# Revit family: Bosch_MechanicalEquipment_GasCondensingBoiler_Condens7000FCascadePair_LowOutput
name_source: partatom
category: Mechanical Equipment
revit_build: Autodesk Revit 2016 (Build: 20151007_0715(x64)
units: mm (PartAtom-declared; Revit-internal decimal feet)

## family parameters
Always vertical = Yes
Cut with Voids When Loaded = No
OmniClass Number = 23.75.00.00
OmniClass Title = Climate Control (HVAC)
Part Type = Normal
Room Calculation Point = No
Round Connector Dimension = Use Diameter
Shared = No
Work Plane-Based = No

## types (1)
- Bosch_MechanicalEquipment_GasCondensingBoiler_Condens7000FCascadePair_LowOutput
    150kW = No
    200-300kW = Yes
    6Monthly = No
    75-100kW = No
    AccessClearanceBottom = 0 mm  [stored 0 ft]
    AccessClearanceTop = 0 mm  [stored 0 ft]
    AirInletConnectionSize = 160
    AirInletHeight = 163 mm  [stored 0.534777 ft]
    AirInletOffset = 195 mm  [stored 0.639764 ft]
    Annually = Annual Service
    Assembly Code = D3020100
    AssetType = Fixed
    BIMObjectName = Bosch_MechanicalEquipment_GasCondensingBoilerCascadePair_Condens7000F_600kW
    BMSLinks = Yes
    BespokeTimeframe = No
    BoilerType1 = Bosch_MechanicalEquipment_GasCondensingBoiler_Condens7000FSingle_LowOutput : 300kW (LH)
    BoilerType2 = Bosch_MechanicalEquipment_GasCondensingBoiler_Condens7000FSingle_LowOutput : 300kW (RH)
    BuildingRegulationsSeasonalEfficiency = 96.8
    BurnerConfiguration = Integral
    CEApproval = CE-0085CS0098
    ClassificationName = Uniclass2015
    ClassificationValue = Pr_60_60_08_34
    CodePerformance = EU Regulations 811/2013, 812/2013, 813/2013 and 814/2013 of Directive 2010/30/EU
    Color = Grey
    CondensateDia = 20 mm  [stored 0.0656168 ft]
    CondensateDrainSize = DN20
    CondensateDrainType = Pipe
    CondensateHeight = 177 mm  [stored 0.580709 ft]
    CondensateOffset = 209 mm  [stored 0.685696 ft]
    Configuration = Cascade Pair Boiler
    Constituents = Aluminium, steel, polymers
    ControlOptions = MX25 or CC 8313
    ControlType = EMS, Volt free, 0-10VDC
    Daily = No
    Description = Higher fuel efficiency, lower environmental impact and exemplary economy - the condensing boiler Condens 7000 F offers you a new level of efficiency in condensing technology. Suitable for multi-family homes and commercial properties, they are the ideal solution for large projects from 75 to 600 kW.
    DocumentationLiterature = https://www.bosch-thermotechnology.com
    DrainCockDia = 15 mm  [stored 0.0492126 ft]
    DrainCockHeight = 498 mm
    DrainConnectionSize = 1/2"
    DrainConnectionType = Threaded
    DurationUnit = Years
    ExpectedLife = 20
    ExternalMaterial = Steel
    Features = Optional retrofittable internet interface and the mobile control of Bosch EasyRemote or HomeCom (Pro).
    Finish = Paint
    FlowAndReturnConnectionSize = DN65
    FlowAndReturnConnectionType = Flange
    FlowOutDepth = 49 mm  [stored 0.160761 ft]
    FlowOutDia = 65 mm  [stored 0.213255 ft]
    FlueOrAirIntakeClassification = OF or RS
    FlueRearDepth = 63 mm
    FlueRearHeight = 765 mm  [stored 2.50984 ft]
    Frequency = 50Hz
    FuelConnectionSize = 1 1/4"
    FuelConnectionType = Threaded
    FullLoadCurrent = 1.46
    FuseRating = 6.3/10
    GasConsumptionRate = 60.4m3/h
    GasHeightOffset = 139 mm  [stored 0.456037 ft]
    GasInDia = 32 mm  [stored 0.104987 ft]
    GasOffset = 478 mm  [stored 1.56824 ft]
    GrossWeight = 544.00 kg
    HasMaintenanceLane = No
    HeatExchangerMaterial = Aluminium
    HeaterOperation = Sealed System
    Height = 1470 mm  [stored 4.82283 ft]
    IPRating = IPX0D
    IfcExportAs = IfcBoiler
    IfcExportType = IfcBoilerTypeEnum.GAS
    Interlocks = Yes
    Keynote = T20/320
    LH = Yes
    LHDrainCockOffset = 495 mm  [stored 1.62402 ft]
    LHFlowOffset = 485 mm  [stored 1.59121 ft]
    LHVSLOffset = 495 mm  [stored 1.62402 ft]
    Length = 1250 mm  [stored 4.10105 ft]
    LocationOfManufacturer = Germany
    MaintenanceRequired0-300Hrs = No
    MaintenanceRequired1001-2000Hrs = No
    MaintenanceRequired2001-4000Hrs = No
    MaintenanceRequired301-600Hrs = No
    MaintenanceRequired4001-8000Hrs = No
    MaintenanceRequired601-1000Hrs = No
    MaintenanceRequired8001-12000Hrs = No
    Manufacturer = Bosch Thermotechnology
    ManufacturerName = Bosch Thermotechnology
    Material = Aluminium, steel, stainless steel,  polymers
    MaximumGasInletPressure = 25mbar
    MaximumOperatingPressure = 6bar
    MaximumPowerConsumption = 672Watts
    MinimumGasInletPressure = 17mbar
    MinimumOperatingPressure = 0.8bar
    MinimumPowerConsumption = 48Watts
    Model = Condens 7000F Gas Condensing Boiler (Cascade Pair)
    ModelNumber = 600kW (No Maintenance Lane)
    ModelReference = Condens 7000F Gas Condensing Boiler (Cascade Pair)
    Monthly = No
    Mounting = Floor Standing
    NBSDescription = Gas fired condensing boilers
    NBSObjectName = Bosch - Gas fired condensing boilers
    NBSReference = 90-40-05/340
    NOxEmissions = 40mg/kWh
    NominalGasInletPressure = 20mbar
    NominalHeight = 1470 mm  [stored 4.82283 ft]
    NominalLength = 1250 mm  [stored 4.10105 ft]
    O&MManual = https://www.bosch-thermotechnology.com
    PrimaryFuel = Gas - NG
    ProductLiterature = https://www.bosch-thermotechnology.com
    ProductModelNumber = 600kW (No Maintenance Lane)
    ProductRange = Condens 7000F Cascade Pair
    ProductionYear = 2017
    Quaterly = No
    RH = No
    RHDrainCockOffset = 190 mm
    RHFlowOffset = 200 mm  [stored 0.656168 ft]
    RHVSLOffset = 190 mm
    RatedCriteria = 50/30
    RatedEfficiencyAtFullLoad = 108
    RatedEfficiencyAtPartLoad = 105
    RatedOutput = 600kW
    ReferencedStandard = BS EN
    ReturnInDia = 65 mm  [stored 0.213255 ft]
    ReturnInHeight = 555 mm  [stored 1.82087 ft]
    SafetyValveConnectionSize = 1 1/4"
    SafetyValveConnectionType = Threaded
    SecondaryFuel = No Secondary Fuel
    Shape = Rectangular (Horiztonal)
    ShippingWeight = 388.00 kg
    Size = 1340x1250x1470mm
    SoundPressureLevel = 63
    StartingCurrent = 0.208
    SupplyPhase = Single
    TurndownRatio = 11.67
    Type = Space Heating
    Type Comments = 600kW (No Maintenance Lane)
    TypeName = 600kW (No Maintenance Lane)
    URL = https://www.bosch-thermotechnology.com
    UnitWidth = 670 mm  [stored 2.19816 ft]
    VSLDepth = 53 mm  [stored 0.173885 ft]
    VSLDia = 32 mm  [stored 0.104987 ft]
    Voltage = 230
    WarrantyDurationLabor = 0
    WarrantyDurationParts = 0
    WarrantyDurationUnit = Years
    WarrantyID = Serial number and end user registration
    WaterContent = 88
    Weekly = System Pressure Check
    _BSBibleVersion = 15
    _BimSpecGuid = 0
    _CurrentRevision = 1
    _DistributedBy = www.bimstore.co.uk

note: [stored X ft] marks values corroborated as IEEE doubles in the binary element streams (Revit-internal decimal feet)

## geometry (parser evidence)
native form markers: Blend x8, Sweep x28
no freeform markers — native parametric forms only
